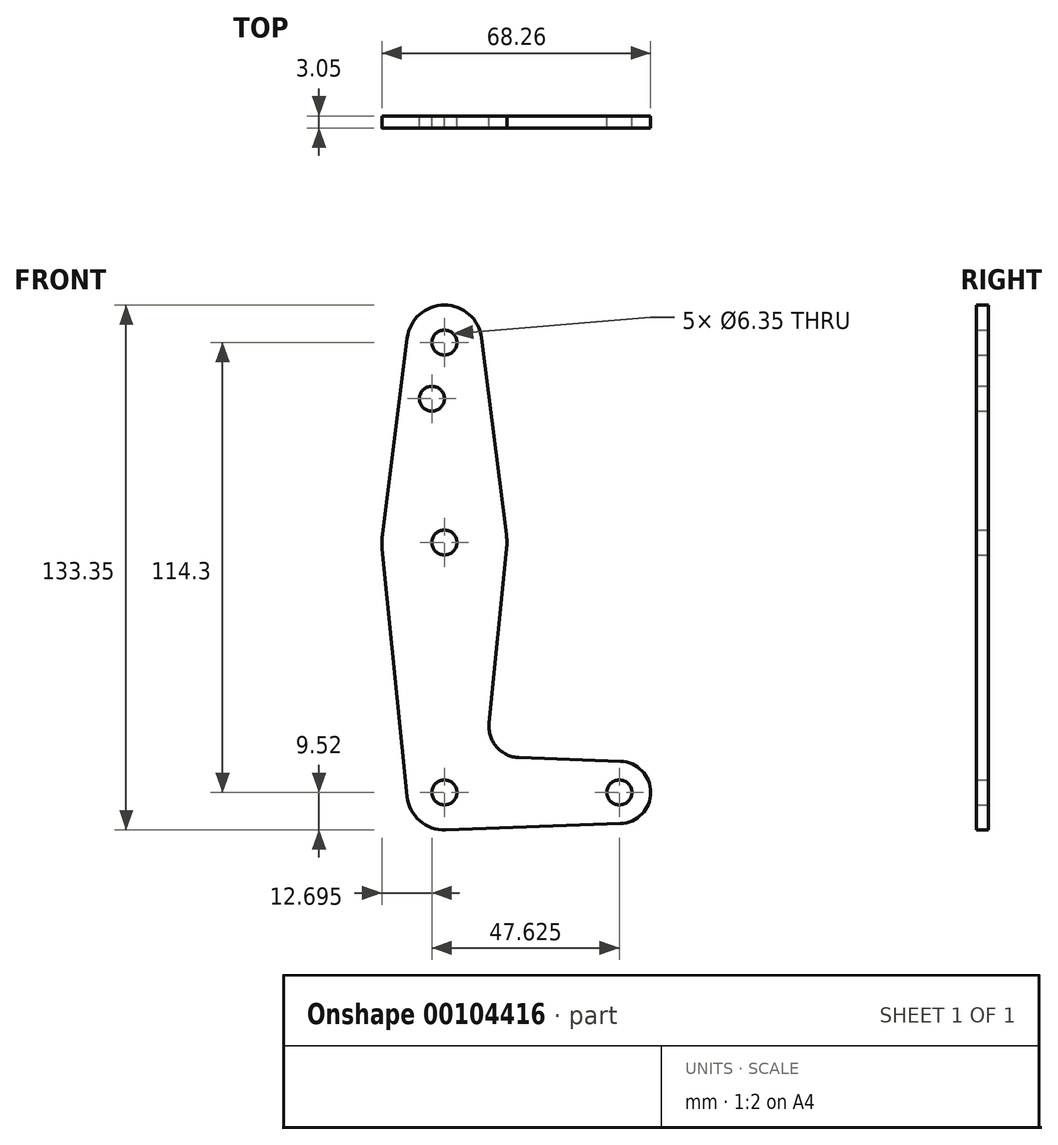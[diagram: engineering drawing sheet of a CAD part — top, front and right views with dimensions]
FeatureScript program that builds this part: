
annotation { "Feature Type Name" : "Feature", "Feature Type Description" : "" }
export const myFeature = defineFeature(function(context is Context, id is Id, definition is map)
    precondition{}
    {
        {
            var Q0;
            Q0=qCreatedBy(makeId("Front.planeOp"),FACE);
            var sketch = newSketch(context, id + "F0", { "sketchPlane" : qUnion([Q0])});
            skCircle(sketch, "E0", {"center": v(0, 114.3) * mm, "radius": 9.53 * mm});
            skCircle(sketch, "E1", {"center": v(0, 63.5) * mm, "radius": 15.88 * mm});
            skCircle(sketch, "E2", {"center": v(0, 0) * mm, "radius": 9.53 * mm});
            skCircle(sketch, "E3", {"center": v(44.45, 0) * mm, "radius": 7.94 * mm});
            skLineSegment(sketch, "E4", {"start": v(-9.45, 115.5) * mm, "end": v(-15.75, 65.48) * mm});
            skLineSegment(sketch, "E5", {"start": v(9.45, 115.5) * mm, "end": v(15.75, 65.48) * mm});
            skLineSegment(sketch, "E6", {"start": v(-15.8, 61.91) * mm, "end": v(-9.48, -0.95) * mm});
            skLineSegment(sketch, "E7", {"start": v(11.34, 17.6) * mm, "end": v(15.8, 61.91) * mm});
            skLineSegment(sketch, "E8", {"start": v(18.97, 8.85) * mm, "end": v(44.73, 7.93) * mm});
            skLineSegment(sketch, "E9", {"start": v(0.34, -9.52) * mm, "end": v(44.73, -7.93) * mm});
            skCircle(sketch, "E10", {"center": v(0, 114.3) * mm, "radius": 3.18 * mm});
            skCircle(sketch, "E11", {"center": v(0, 63.5) * mm, "radius": 3.18 * mm});
            skCircle(sketch, "E12", {"center": v(0, 0) * mm, "radius": 3.18 * mm});
            skCircle(sketch, "E13", {"center": v(44.45, 0) * mm, "radius": 3.18 * mm});
            skCircle(sketch, "E14", {"center": v(-3.17, 100.03) * mm, "radius": 3.18 * mm});
            skArc(sketch, "E15.filletArc", {"start": v(11.34, 17.6) * mm, "mid": v(13.26, 11.57) * mm, "end": v(18.97, 8.85) * mm});
            skSolve(sketch);
        }
        {
            var Q0;
            Q0 = qSketchRegion(id + "F0", true);
            extrude(context, id + "F1", {"entities" : qUnion([Q0]), "depth" : 3.05 * mm});
        }
    });
